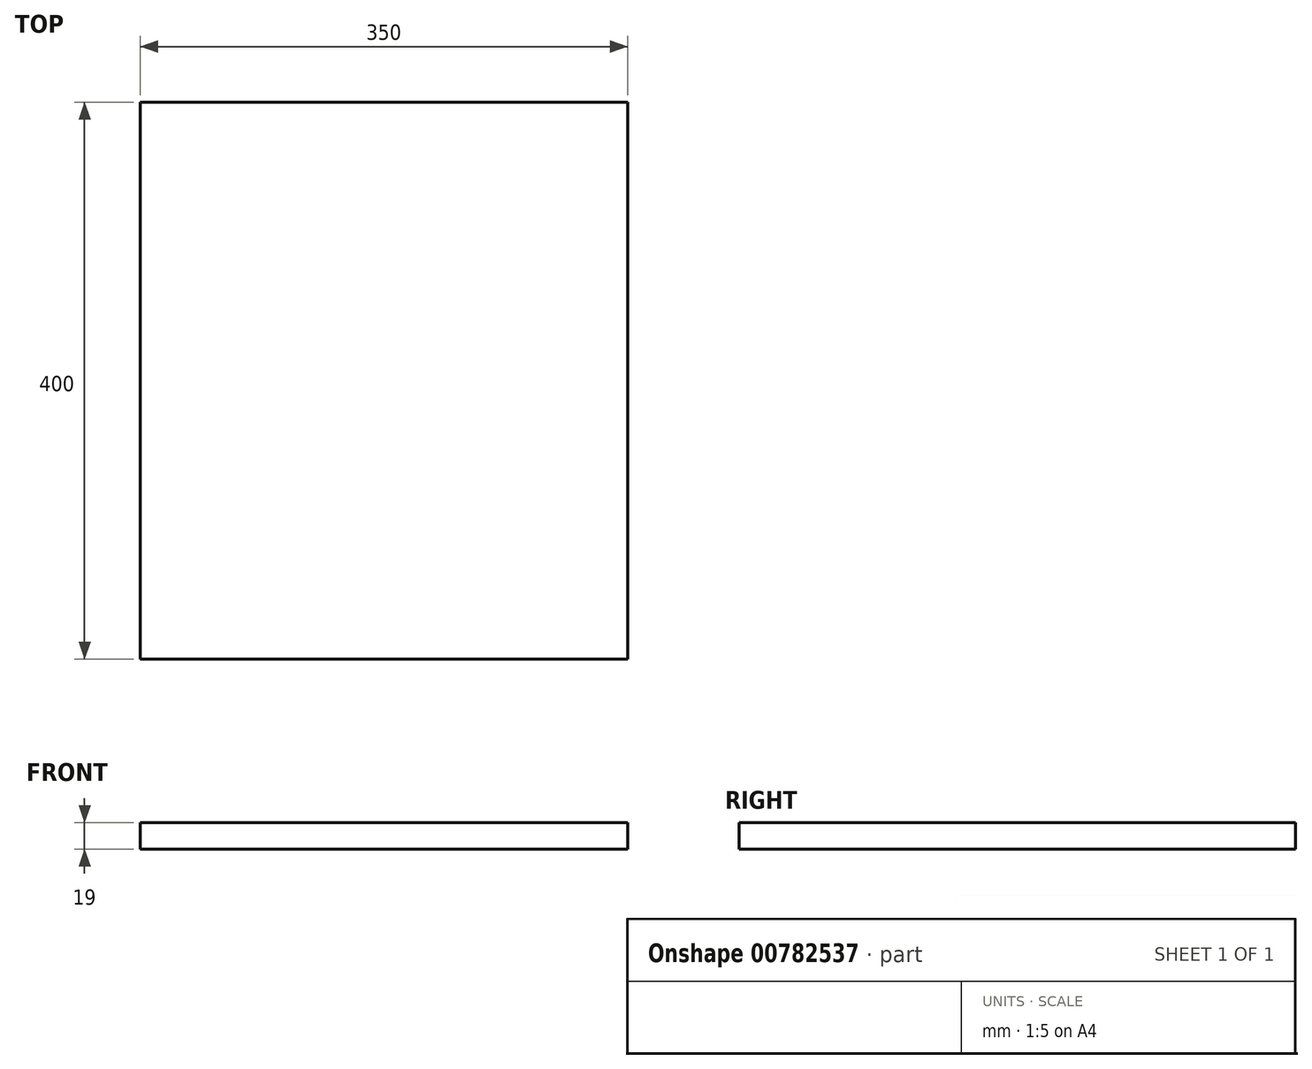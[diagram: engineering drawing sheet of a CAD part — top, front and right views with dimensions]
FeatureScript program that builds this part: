
annotation { "Feature Type Name" : "Feature", "Feature Type Description" : "" }
export const myFeature = defineFeature(function(context is Context, id is Id, definition is map)
    precondition{}
    {
        {
            var Q0;
            Q0=qCreatedBy(makeId("Top.planeOp"),FACE);
            var sketch = newSketch(context, id + "F0", { "sketchPlane" : qUnion([Q0])});
            skLineSegment(sketch, "E0.bottom", {"start": v(-175, 200) * mm, "end": v(175, 200) * mm});
            skLineSegment(sketch, "E0.top", {"start": v(-175, -200) * mm, "end": v(175, -200) * mm});
            skLineSegment(sketch, "E0.left", {"start": v(-175, 200) * mm, "end": v(-175, -200) * mm});
            skLineSegment(sketch, "E0.right", {"start": v(175, 200) * mm, "end": v(175, -200) * mm});
            skPoint(sketch, "E0.middle", {"position": v(0, 0) * mm});
            skSolve(sketch);
        }
        {
            var Q0;
            Q0 = qSketchRegion(id + "F0", true);
            extrude(context, id + "F1", {"entities" : qUnion([Q0]), "depth" : 19 * mm, "offsetDistance" : 25 * mm});
        }
    });
